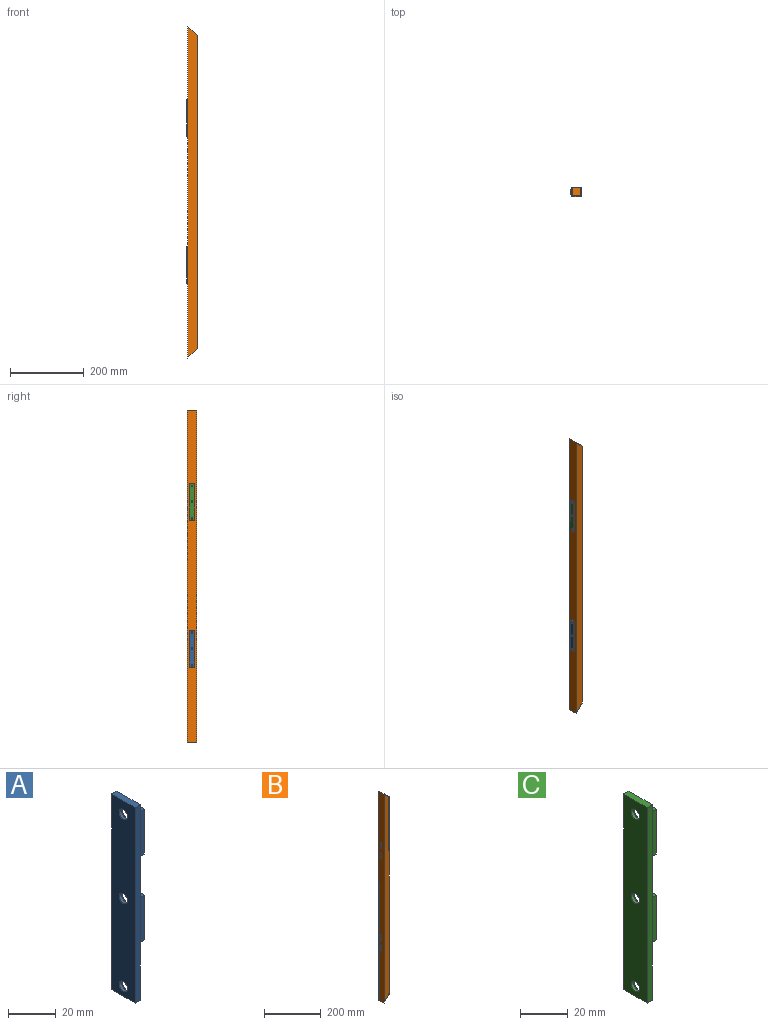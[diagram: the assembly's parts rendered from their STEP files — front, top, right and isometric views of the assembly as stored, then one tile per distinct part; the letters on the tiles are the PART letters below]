
ASSEMBLY  parts=3 mates=2
PART A: 26 faces, bbox 11x14x100 mm
  f0: plane 100x14mm, normal (1,0,0), area 1159.2mm2, adj f1,f3,f4,f5,f7,f9,f11,f12
  f1: plane 14x3mm, normal (0,0,1), area 42mm2, adj f0,f2,f4,f5
  f2: plane 100x14mm, normal (-1,0,0), area 1341.1mm2, adj f1,f3,f4,f5,f6,f8,f10
  f3: plane 14x3mm, normal (0,0,-1), area 42mm2, adj f0,f2,f4,f5
  f4: plane 100x3mm, normal (0,-1,0), area 300mm2, adj f0,f1,f2,f3
  f5: plane 100x3mm, normal (0,1,0), area 300mm2, adj f0,f1,f2,f3
  f6: cylinder r=2.5mm len=5mm, axis (1,0,0), area 23.6mm2, adj f2,f7
  f7: cone r=2.5mm half-angle=45deg, axis (1,0,0), area 43.3mm2, adj f0,f6
  f8: cylinder r=2.5mm len=5mm, axis (1,0,0), area 23.6mm2, adj f2,f9
  f9: cone r=2.5mm half-angle=45deg, axis (1,0,0), area 43.3mm2, adj f0,f8
  f10: cylinder r=2.5mm len=5mm, axis (1,0,0), area 23.6mm2, adj f2,f11
  f11: cone r=2.5mm half-angle=45deg, axis (1,0,0), area 43.3mm2, adj f0,f10
  f12: plane 8x3mm, normal (0,0,-1), area 24mm2, adj f0,f13,f17,f18
  f13: plane 23x3mm, normal (1,0,0), area 69mm2, adj f12,f14,f17,f18
  f14: plane 5x3mm, normal (0,0,1), area 15mm2, adj f13,f15,f17,f18
  f15: plane 8x3mm, normal (-0.99,0,0.12), area 24.2mm2, adj f14,f16,f17,f18
  f16: plane 3x2mm, normal (0,0,1), area 6mm2, adj f0,f15,f17,f18
  f17: plane 23x8mm, normal (0,-1,0), area 164mm2, adj f0,f12,f13,f14,f15,f16
  f18: plane 23x8mm, normal (0,1,0), area 164mm2, adj f0,f12,f13,f14,f15,f16
  f19: plane 8x3mm, normal (0,0,-1), area 24mm2, adj f0,f20,f24,f25
  f20: plane 23x3mm, normal (1,0,0), area 69mm2, adj f19,f21,f24,f25
  f21: plane 5x3mm, normal (0,0,1), area 15mm2, adj f20,f22,f24,f25
  f22: plane 8x3mm, normal (-0.99,0,0.12), area 24.2mm2, adj f21,f23,f24,f25
  f23: plane 3x2mm, normal (0,0,1), area 6mm2, adj f0,f22,f24,f25
  f24: plane 23x8mm, normal (0,-1,0), area 164mm2, adj f0,f19,f20,f21,f22,f23
  f25: plane 23x8mm, normal (0,1,0), area 164mm2, adj f0,f19,f20,f21,f22,f23
PART B: 28 faces, bbox 25.4x25.4x900 mm
  f0: plane 900x25.4mm, normal (-1,0,0), area 22360mm2, adj f1,f2,f4,f5,f6,f7,f8,f9
  f1: plane 25.4x25.4mm, normal (0.71,0,-0.71), area 912.4mm2, adj f0,f3,f4,f5
  f2: plane 25.4x25.4mm, normal (0.71,0,0.71), area 912.4mm2, adj f0,f3,f4,f5
  f3: plane 849.2x25.4mm, normal (1,0,0), area 21569.7mm2, adj f1,f2,f4,f5
  f4: plane 900x25.4mm, normal (0,1,0), area 22214.8mm2, adj f0,f1,f2,f3
  f5: plane 900x25.4mm, normal (0,-1,0), area 22214.8mm2, adj f0,f1,f2,f3
  f6: plane 25x1.5mm, normal (0,1,0), area 37.5mm2, adj f0,f7,f9,f22
  f7: plane 5x1.5mm, normal (0,0,-1), area 7.5mm2, adj f0,f6,f8,f22
  f8: plane 25x1.5mm, normal (0,-1,0), area 37.5mm2, adj f0,f7,f9,f22
  f9: plane 5x1.5mm, normal (0,0,1), area 7.5mm2, adj f0,f6,f8,f22
  f10: plane 25x1.5mm, normal (0,1,0), area 37.5mm2, adj f0,f11,f13,f22
  f11: plane 5x1.5mm, normal (0,0,-1), area 7.5mm2, adj f0,f10,f12,f22
  f12: plane 25x1.5mm, normal (0,-1,0), area 37.5mm2, adj f0,f11,f13,f22
  f13: plane 5x1.5mm, normal (0,0,1), area 7.5mm2, adj f0,f10,f12,f22
  f14: plane 25x1.5mm, normal (0,1,0), area 37.5mm2, adj f0,f15,f17,f22
  f15: plane 5x1.5mm, normal (0,0,-1), area 7.5mm2, adj f0,f14,f16,f22
  f16: plane 25x1.5mm, normal (0,-1,0), area 37.5mm2, adj f0,f15,f17,f22
  f17: plane 5x1.5mm, normal (0,0,1), area 7.5mm2, adj f0,f14,f16,f22
  f18: plane 25x1.5mm, normal (0,1,0), area 37.5mm2, adj f0,f19,f21,f22
  f19: plane 5x1.5mm, normal (0,0,-1), area 7.5mm2, adj f0,f18,f20,f22
  f20: plane 25x1.5mm, normal (0,-1,0), area 37.5mm2, adj f0,f19,f21,f22
  f21: plane 5x1.5mm, normal (0,0,1), area 7.5mm2, adj f0,f18,f20,f22
  f22: plane 892.76x22.4mm, normal (1,0,0), area 19497.8mm2, adj f6,f7,f8,f9,f10,f11,f12,f13
  f23: plane 22.4x22.4mm, normal (-0.71,0,-0.71), area 709.6mm2, adj f22,f24,f25,f26
  f24: plane 847.96x22.4mm, normal (-1,0,0), area 18994.2mm2, adj f23,f25,f26,f27
  f25: plane 892.76x22.4mm, normal (0,1,0), area 19496mm2, adj f22,f23,f24,f27
  f26: plane 892.76x22.4mm, normal (0,-1,0), area 19496mm2, adj f22,f23,f24,f27
  f27: plane 22.4x22.4mm, normal (-0.71,0,0.71), area 709.6mm2, adj f22,f24,f25,f26
PART C: 26 faces, bbox 11x14x100 mm
  f0: plane 100x14mm, normal (1,0,0), area 1159.2mm2, adj f1,f3,f4,f5,f7,f9,f11,f12
  f1: plane 14x3mm, normal (0,0,1), area 42mm2, adj f0,f2,f4,f5
  f2: plane 100x14mm, normal (-1,0,0), area 1341.1mm2, adj f1,f3,f4,f5,f6,f8,f10
  f3: plane 14x3mm, normal (0,0,-1), area 42mm2, adj f0,f2,f4,f5
  f4: plane 100x3mm, normal (0,-1,0), area 300mm2, adj f0,f1,f2,f3
  f5: plane 100x3mm, normal (0,1,0), area 300mm2, adj f0,f1,f2,f3
  f6: cylinder r=2.5mm len=5mm, axis (1,0,0), area 23.6mm2, adj f2,f7
  f7: cone r=2.5mm half-angle=45deg, axis (1,0,0), area 43.3mm2, adj f0,f6
  f8: cylinder r=2.5mm len=5mm, axis (1,0,0), area 23.6mm2, adj f2,f9
  f9: cone r=2.5mm half-angle=45deg, axis (1,0,0), area 43.3mm2, adj f0,f8
  f10: cylinder r=2.5mm len=5mm, axis (1,0,0), area 23.6mm2, adj f2,f11
  f11: cone r=2.5mm half-angle=45deg, axis (1,0,0), area 43.3mm2, adj f0,f10
  f12: plane 8x3mm, normal (0,0,-1), area 24mm2, adj f0,f13,f17,f18
  f13: plane 23x3mm, normal (1,0,0), area 69mm2, adj f12,f14,f17,f18
  f14: plane 5x3mm, normal (0,0,1), area 15mm2, adj f13,f15,f17,f18
  f15: plane 8x3mm, normal (-0.99,0,0.12), area 24.2mm2, adj f14,f16,f17,f18
  f16: plane 3x2mm, normal (0,0,1), area 6mm2, adj f0,f15,f17,f18
  f17: plane 23x8mm, normal (0,-1,0), area 164mm2, adj f0,f12,f13,f14,f15,f16
  f18: plane 23x8mm, normal (0,1,0), area 164mm2, adj f0,f12,f13,f14,f15,f16
  f19: plane 8x3mm, normal (0,0,-1), area 24mm2, adj f0,f20,f24,f25
  f20: plane 23x3mm, normal (1,0,0), area 69mm2, adj f19,f21,f24,f25
  f21: plane 5x3mm, normal (0,0,1), area 15mm2, adj f20,f22,f24,f25
  f22: plane 8x3mm, normal (-0.99,0,0.12), area 24.2mm2, adj f21,f23,f24,f25
  f23: plane 3x2mm, normal (0,0,1), area 6mm2, adj f0,f22,f24,f25
  f24: plane 23x8mm, normal (0,-1,0), area 164mm2, adj f0,f19,f20,f21,f22,f23
  f25: plane 23x8mm, normal (0,1,0), area 164mm2, adj f0,f19,f20,f21,f22,f23
PLACE A t=(38.25,-17.63,-0.75)mm
PLACE B t=(26.25,-17.63,-3.75)mm
PLACE C t=(38.25,-17.63,-2.75)mm
MATE fastened C.f0 <-> B.f0  axis (1,0,0) through (13.55,-17.63,230.25)mm
MATE fastened A.f0 <-> B.f0  axis (1,0,0) through (13.55,-17.63,-167.75)mm
